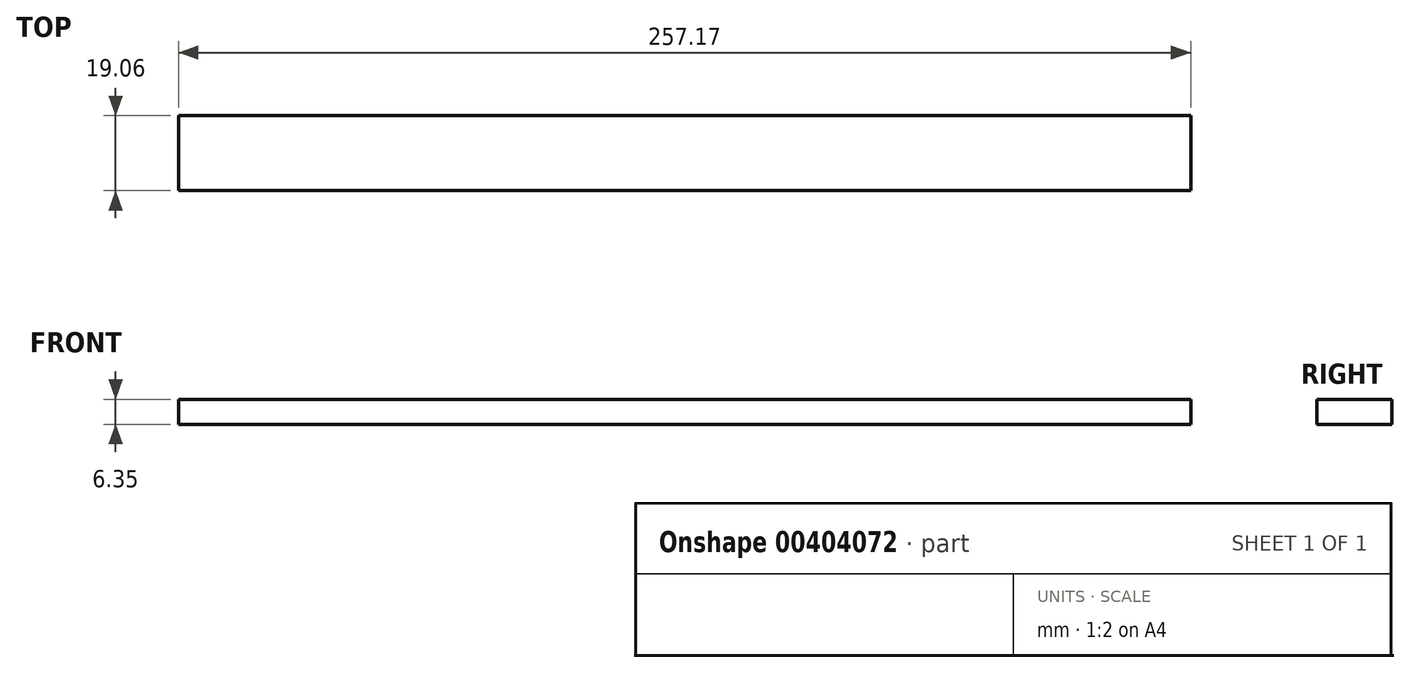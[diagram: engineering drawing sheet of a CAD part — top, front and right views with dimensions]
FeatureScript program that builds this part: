
annotation { "Feature Type Name" : "Feature", "Feature Type Description" : "" }
export const myFeature = defineFeature(function(context is Context, id is Id, definition is map)
    precondition{}
    {
        {
            var Q0;
            Q0=qCreatedBy(makeId("Top.planeOp"),FACE);
            var sketch = newSketch(context, id + "F0", { "sketchPlane" : qUnion([Q0])});
            skLineSegment(sketch, "E0.bottom", {"start": v(64.3, 9.53) * mm, "end": v(-64.3, 9.53) * mm});
            skLineSegment(sketch, "E0.top", {"start": v(64.3, -9.53) * mm, "end": v(-64.3, -9.53) * mm});
            skLineSegment(sketch, "E0.left", {"start": v(64.3, 9.53) * mm, "end": v(64.3, -9.53) * mm});
            skLineSegment(sketch, "E0.right", {"start": v(-64.3, 9.53) * mm, "end": v(-64.3, -9.53) * mm});
            skPoint(sketch, "E0.middle", {"position": v(0, 0) * mm});
            skPoint(sketch, "E1.MirrorP", {"position": v(128.59, 0) * mm});
            skPoint(sketch, "E2.MirrorP", {"position": v(-257.18, 0) * mm});
            skPoint(sketch, "E3.MirrorP", {"position": v(-128.59, 0) * mm});
            skLineSegment(sketch, "E4.MirrorCS", {"start": v(-192.88, 9.52) * mm, "end": v(-192.88, -9.53) * mm});
            skLineSegment(sketch, "E5.MirrorCS", {"start": v(-192.88, -9.53) * mm, "end": v(-64.3, -9.53) * mm});
            skLineSegment(sketch, "E6.MirrorCS", {"start": v(-192.88, 9.52) * mm, "end": v(-64.3, 9.53) * mm});
            skSolve(sketch);
        }
        {
            var Q0;
            Q0=makeQuery(id+"F0.imprint","IMPRINT",FACE,{"disambiguationData":[TD([[makeQuery(id+"F0.imprint","IMPRINT",EDGE,{"derivedFrom":sQuery(id+"F0.wireOp",EDGE,"E0.bottom")}),1.0]])]});
            var Q1;
            Q1=makeQuery(id+"F0.imprint","IMPRINT",FACE,{"disambiguationData":[TD([[makeQuery(id+"F0.imprint","IMPRINT",EDGE,{"derivedFrom":sQuery(id+"F0.wireOp",EDGE,"E0.right")}),-1.0]])]});
            extrude(context, id + "F1", {"entities" : qUnion([Q0, Q1]), "depth" : 6.35 * mm});
        }
    });
